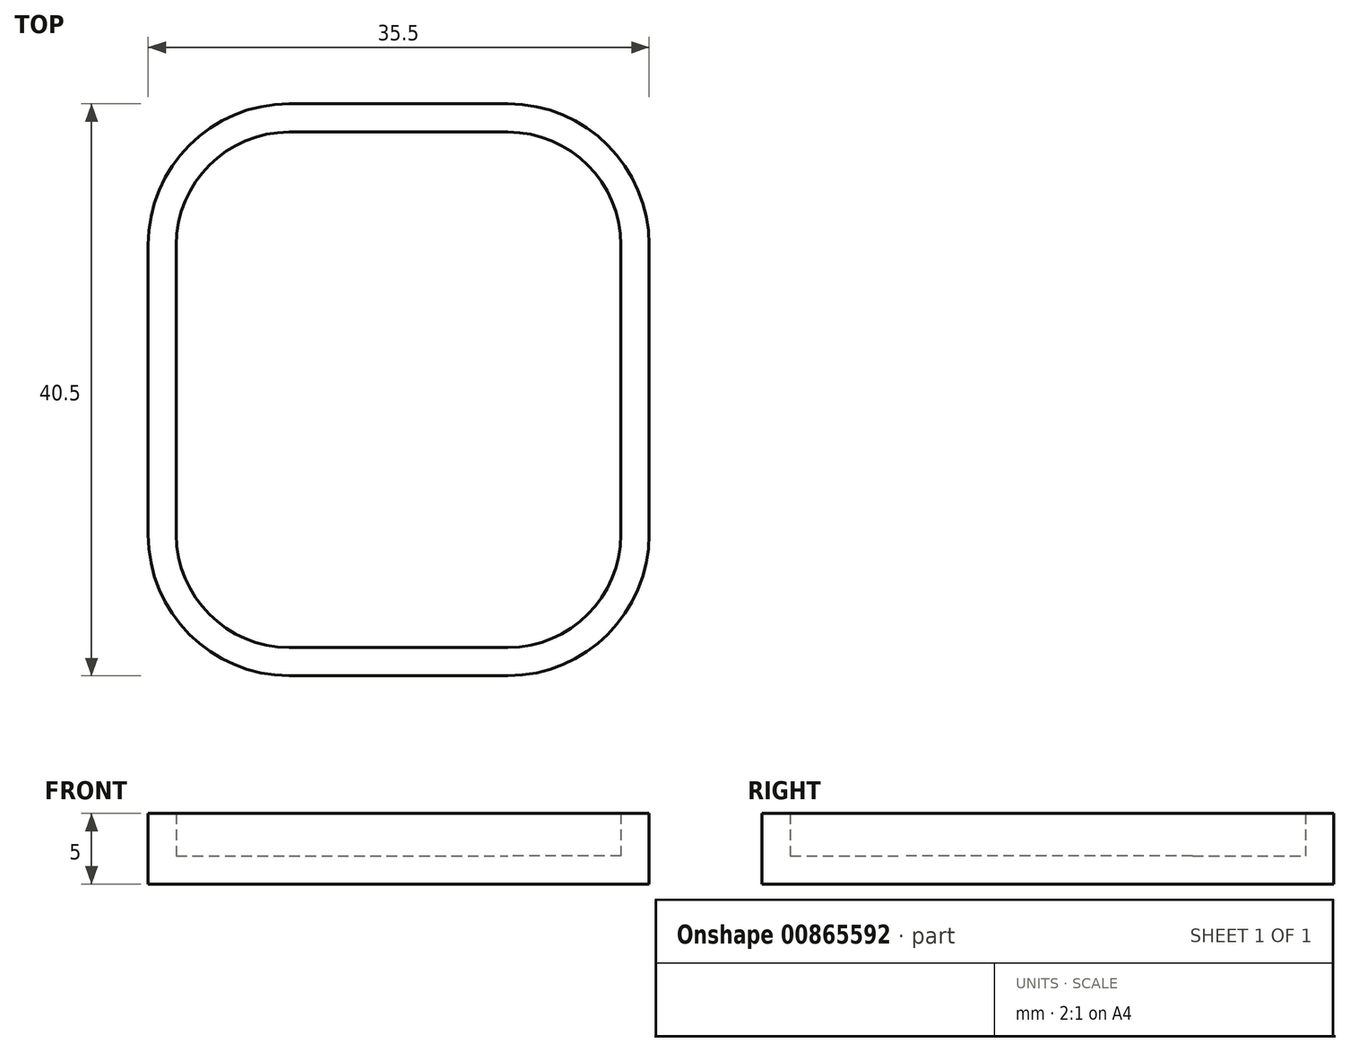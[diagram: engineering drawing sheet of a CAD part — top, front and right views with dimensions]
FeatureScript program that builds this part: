
annotation { "Feature Type Name" : "Feature", "Feature Type Description" : "" }
export const myFeature = defineFeature(function(context is Context, id is Id, definition is map)
    precondition{}
    {
        {
            var Q0;
            Q0=qCreatedBy(makeId("Top.planeOp"),FACE);
            var sketch = newSketch(context, id + "F0", { "sketchPlane" : qUnion([Q0])});
            skLineSegment(sketch, "E0.bottom", {"start": v(-6.21, 1.01) * mm, "end": v(-21.71, 1.01) * mm});
            skLineSegment(sketch, "E0.top", {"start": v(-6.21, 37.51) * mm, "end": v(-21.71, 37.51) * mm});
            skLineSegment(sketch, "E0.left", {"start": v(1.79, 9.01) * mm, "end": v(1.79, 29.51) * mm});
            skLineSegment(sketch, "E0.right", {"start": v(-29.71, 9.01) * mm, "end": v(-29.71, 29.51) * mm});
            skLineSegment(sketch, "E1.bottom", {"start": v(-6.21, -0.99) * mm, "end": v(-21.71, -0.99) * mm});
            skLineSegment(sketch, "E1.top", {"start": v(-6.21, 39.51) * mm, "end": v(-21.71, 39.51) * mm});
            skLineSegment(sketch, "E1.left", {"start": v(3.79, 9.01) * mm, "end": v(3.79, 29.51) * mm});
            skLineSegment(sketch, "E1.right", {"start": v(-31.71, 9.01) * mm, "end": v(-31.71, 29.51) * mm});
            skPoint(sketch, "E2.visualSharp", {"position": v(-29.71, 37.51) * mm});
            skArc(sketch, "E2.filletArc", {"start": v(-21.71, 37.51) * mm, "mid": v(-27.37, 35.17) * mm, "end": v(-29.71, 29.51) * mm});
            skPoint(sketch, "E3.visualSharp", {"position": v(1.79, 37.51) * mm});
            skArc(sketch, "E3.filletArc", {"start": v(1.79, 29.51) * mm, "mid": v(-0.55, 35.17) * mm, "end": v(-6.21, 37.51) * mm});
            skPoint(sketch, "E4.visualSharp", {"position": v(1.79, 1.01) * mm});
            skArc(sketch, "E4.filletArc", {"start": v(-6.21, 1.01) * mm, "mid": v(-0.55, 3.36) * mm, "end": v(1.79, 9.01) * mm});
            skPoint(sketch, "E5.visualSharp", {"position": v(-29.71, 1.01) * mm});
            skArc(sketch, "E5.filletArc", {"start": v(-29.71, 9.01) * mm, "mid": v(-27.37, 3.36) * mm, "end": v(-21.71, 1.01) * mm});
            skPoint(sketch, "E6.visualSharp", {"position": v(-31.71, 39.51) * mm});
            skArc(sketch, "E6.filletArc", {"start": v(-21.71, 39.51) * mm, "mid": v(-28.78, 36.58) * mm, "end": v(-31.71, 29.51) * mm});
            skPoint(sketch, "E7.visualSharp", {"position": v(3.79, 39.51) * mm});
            skArc(sketch, "E7.filletArc", {"start": v(3.79, 29.51) * mm, "mid": v(0.86, 36.58) * mm, "end": v(-6.21, 39.51) * mm});
            skPoint(sketch, "E8.visualSharp", {"position": v(3.79, -0.99) * mm});
            skArc(sketch, "E8.filletArc", {"start": v(-6.21, -0.99) * mm, "mid": v(0.86, 1.94) * mm, "end": v(3.79, 9.01) * mm});
            skPoint(sketch, "E9.visualSharp", {"position": v(-31.71, -0.99) * mm});
            skArc(sketch, "E9.filletArc", {"start": v(-31.71, 9.01) * mm, "mid": v(-28.78, 1.94) * mm, "end": v(-21.71, -0.99) * mm});
            skSolve(sketch);
        }
        {
            var Q0;
            Q0=makeQuery(id+"F0.imprint","IMPRINT",FACE,{"disambiguationData":[TD([[makeQuery(id+"F0.imprint","IMPRINT",EDGE,{"derivedFrom":sQuery(id+"F0.wireOp",EDGE,"E0.bottom")}),1.0]])]});
            var Q1;
            Q1=makeQuery(id+"F0.imprint","IMPRINT",FACE,{"disambiguationData":[TD([[makeQuery(id+"F0.imprint","IMPRINT",EDGE,{"derivedFrom":sQuery(id+"F0.wireOp",EDGE,"E0.bottom")}),-1.0]])]});
            extrude(context, id + "F1", {"entities" : qUnion([Q0, Q1]), "depth" : 2 * mm, "offsetDistance" : 25 * mm});
        }
        {
            var Q0;
            Q0=makeQuery(id+"F0.imprint","IMPRINT",FACE,{"disambiguationData":[TD([[makeQuery(id+"F0.imprint","IMPRINT",EDGE,{"derivedFrom":sQuery(id+"F0.wireOp",EDGE,"E0.bottom")}),1.0]])]});
            extrude(context, id + "F2", {"entities" : qUnion([Q0]), "operationType" : NewBodyOperationType.ADD, "depth" : 5 * mm, "offsetDistance" : 25 * mm});
        }
    });
